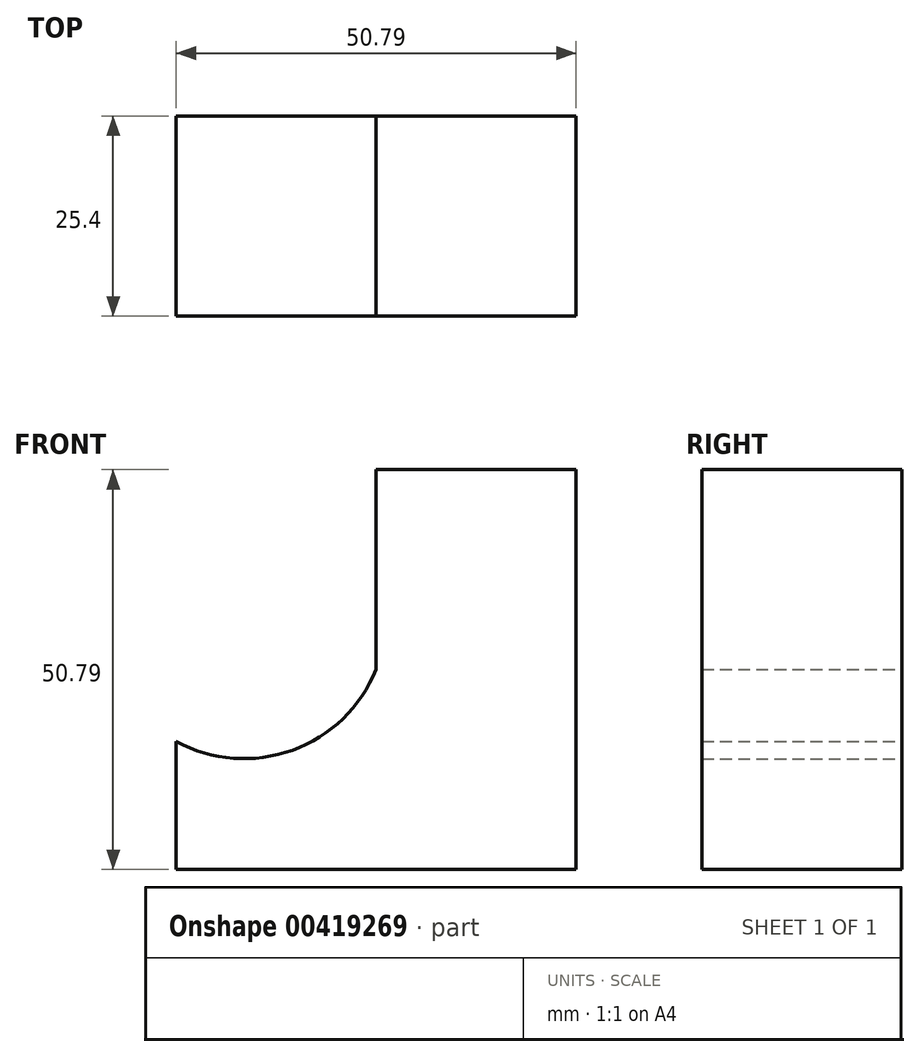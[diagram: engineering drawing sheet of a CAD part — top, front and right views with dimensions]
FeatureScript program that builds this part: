
annotation { "Feature Type Name" : "Feature", "Feature Type Description" : "" }
export const myFeature = defineFeature(function(context is Context, id is Id, definition is map)
    precondition{}
    {
        {
            var Q0;
            Q0=qCreatedBy(makeId("Front.planeOp"),FACE);
            var sketch = newSketch(context, id + "F0", { "sketchPlane" : qUnion([Q0])});
            skLineSegment(sketch, "E0", {"start": v(0, 0) * mm, "end": v(50.8, 0) * mm});
            skLineSegment(sketch, "E1", {"start": v(50.8, 0) * mm, "end": v(50.8, 50.8) * mm});
            skLineSegment(sketch, "E2", {"start": v(50.8, 50.8) * mm, "end": v(25.4, 50.8) * mm});
            skLineSegment(sketch, "E3", {"start": v(25.4, 50.8) * mm, "end": v(25.4, 25.4) * mm});
            skLineSegment(sketch, "E4", {"start": v(0, 0) * mm, "end": v(0, 16.23) * mm});
            skArc(sketch, "E5", {"start": v(0, 16.23) * mm, "mid": v(14.75, 15.14) * mm, "end": v(25.4, 25.4) * mm});
            skSolve(sketch);
        }
        {
            var Q0;
            Q0=makeQuery(id+"F0.imprint","IMPRINT",FACE,{"disambiguationData":[TD([[makeQuery(id+"F0.imprint","IMPRINT",EDGE,{"derivedFrom":sQuery(id+"F0.wireOp",EDGE,"E0")}),1.0]])]});
            extrude(context, id + "F1", {"entities" : qUnion([Q0]), "depth" : 25.4 * mm});
        }
    });
